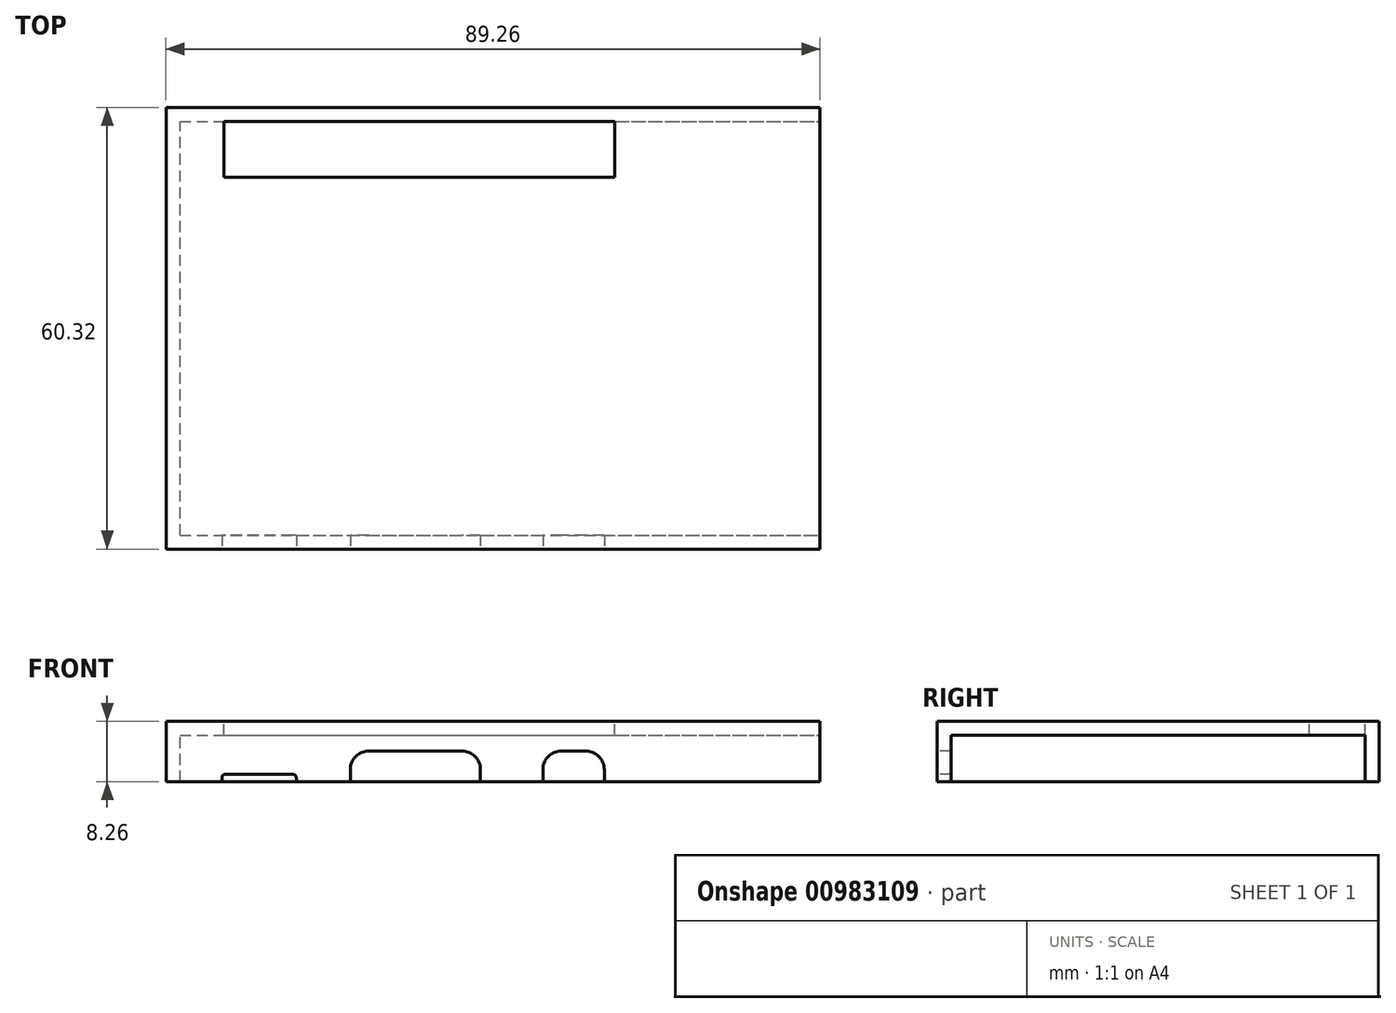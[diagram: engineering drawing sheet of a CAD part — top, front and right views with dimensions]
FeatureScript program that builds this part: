
annotation { "Feature Type Name" : "Feature", "Feature Type Description" : "" }
export const myFeature = defineFeature(function(context is Context, id is Id, definition is map)
    precondition{}
    {
        {
            var Q0;
            Q0=qCreatedBy(makeId("Top.planeOp"),FACE);
            var sketch = newSketch(context, id + "F0", { "sketchPlane" : qUnion([Q0])});
            skLineSegment(sketch, "E0.bottom", {"start": v(-44.63, -30.16) * mm, "end": v(44.63, -30.16) * mm});
            skLineSegment(sketch, "E0.top", {"start": v(-44.63, 30.16) * mm, "end": v(44.63, 30.16) * mm});
            skLineSegment(sketch, "E0.left", {"start": v(-44.63, -30.16) * mm, "end": v(-44.63, 30.16) * mm});
            skLineSegment(sketch, "E0.right", {"start": v(44.63, -30.16) * mm, "end": v(44.63, 30.16) * mm});
            skLineSegment(sketch, "E1", {"start": v(-44.63, 30.16) * mm, "end": v(44.63, -30.16) * mm, "construction": true});
            skSolve(sketch);
        }
        {
            var Q0;
            Q0=makeQuery(id+"F0.imprint","IMPRINT",FACE,{"disambiguationData":[TD([[makeQuery(id+"F0.imprint","IMPRINT",EDGE,{"derivedFrom":sQuery(id+"F0.wireOp",EDGE,"E0.bottom")}),1.0]])]});
            extrude(context, id + "F1", {"entities" : qUnion([Q0]), "depth" : 1.9 * mm, "offsetDistance" : 25.4 * mm});
        }
        {
            var Q0;
            Q0=makeQuery(id+"F1.opExtrude","CAP_FACE",FACE,{"disambiguationData":[OSD([sQuery(id+"F0.wireOp",EDGE,"E0.bottom"),sQuery(id+"F0.wireOp",EDGE,"E0.top"),sQuery(id+"F0.wireOp",EDGE,"E0.left"),sQuery(id+"F0.wireOp",EDGE,"E0.right")])],"isStart":true});
            var sketch = newSketch(context, id + "F2", { "sketchPlane" : qUnion([Q0])});
            skLineSegment(sketch, "E2.0", {"start": v(-42.72, 28.26) * mm, "end": v(44.63, 28.26) * mm});
            skLineSegment(sketch, "E2.1", {"start": v(-42.72, 28.26) * mm, "end": v(-42.72, -28.26) * mm});
            skLineSegment(sketch, "E2.2", {"start": v(-42.72, -28.26) * mm, "end": v(44.63, -28.26) * mm});
            skSolve(sketch);
        }
        {
            var Q0;
            Q0 = qSketchRegion(id + "F2", true);
            var Q1;
            {var subQ2=sQuery(id+"F2.wireOp",EDGE,"E2.0");Q1=makeQuery(id+"F2.imprint","IMPRINT",FACE,{"disambiguationData":[TD([[makeQuery(id+"F2.imprint","IMPRINT",EDGE,{"derivedFrom":subQ2}),1.0]])]});}
            extrude(context, id + "F3", {"entities" : qUnion([Q0, Q1]), "operationType" : NewBodyOperationType.ADD, "depth" : 6.35 * mm, "offsetDistance" : 25.4 * mm});
        }
        {
            var Q0;
            {var subQ0=sQuery(id+"F0.wireOp",EDGE,"E0.bottom");Q0=makeQuery(id+"F3.boolean.opBoolean","MERGE",FACE,{"derivedFrom":[makeQuery(id+"F1.opExtrude","SWEPT_FACE",FACE,{"disambiguationData":[OSD([subQ0])]}),makeQuery(id+"F3.opExtrude","SWEPT_FACE",FACE,{"disambiguationData":[OSD([subQ0])]})]});}
            var sketch = newSketch(context, id + "F4", { "sketchPlane" : qUnion([Q0])});
            skLineSegment(sketch, "E3.bottom", {"start": v(-37, -6.35) * mm, "end": v(-26.85, -6.35) * mm});
            skLineSegment(sketch, "E3.top", {"start": v(-37, 1.9) * mm, "end": v(-26.85, 1.9) * mm});
            skLineSegment(sketch, "E3.left", {"start": v(-37, -6.35) * mm, "end": v(-37, -5.84) * mm});
            skLineSegment(sketch, "E3.right", {"start": v(-26.85, -6.35) * mm, "end": v(-26.85, -5.84) * mm});
            skLineSegment(sketch, "E4", {"start": v(-37, 1.9) * mm, "end": v(-26.85, -6.35) * mm, "construction": true});
            skLineSegment(sketch, "E5.bottom", {"start": v(-19.48, -6.35) * mm, "end": v(-1.7, -6.35) * mm});
            skLineSegment(sketch, "E5.top", {"start": v(-19.48, 1.9) * mm, "end": v(-1.7, 1.9) * mm});
            skLineSegment(sketch, "E5.left", {"start": v(-19.48, -6.35) * mm, "end": v(-19.48, -4.7) * mm});
            skLineSegment(sketch, "E5.right", {"start": v(-1.7, -6.35) * mm, "end": v(-1.7, -4.7) * mm});
            skLineSegment(sketch, "E6.bottom", {"start": v(6.8, -6.35) * mm, "end": v(15.2, -6.35) * mm});
            skLineSegment(sketch, "E6.top", {"start": v(6.8, 1.9) * mm, "end": v(15.2, 1.9) * mm});
            skLineSegment(sketch, "E6.left", {"start": v(6.8, -6.35) * mm, "end": v(6.8, -4.7) * mm});
            skLineSegment(sketch, "E6.right", {"start": v(15.2, -6.35) * mm, "end": v(15.2, -4.7) * mm});
            skLineSegment(sketch, "E7", {"start": v(-19.48, 1.9) * mm, "end": v(-1.7, -6.35) * mm, "construction": true});
            skLineSegment(sketch, "E8", {"start": v(6.8, 1.9) * mm, "end": v(15.2, -6.35) * mm, "construction": true});
            skLineSegment(sketch, "E9", {"start": v(11, -2.22) * mm, "end": v(-44.63, -2.22) * mm, "construction": true});
            skPoint(sketch, "E10", {"position": v(-31.93, -2.22) * mm});
            skPoint(sketch, "E11", {"position": v(-10.6, -2.22) * mm});
            skLineSegment(sketch, "E12", {"start": v(-27.35, -5.33) * mm, "end": v(-36.5, -5.33) * mm});
            skLineSegment(sketch, "E13", {"start": v(-16.94, -2.16) * mm, "end": v(-4.24, -2.16) * mm});
            skLineSegment(sketch, "E14", {"start": v(12.65, -2.16) * mm, "end": v(9.35, -2.16) * mm});
            skArc(sketch, "E15.filletArc", {"start": v(-36.5, -5.33) * mm, "mid": v(-36.86, -5.48) * mm, "end": v(-37, -5.84) * mm});
            skArc(sketch, "E16.filletArc", {"start": v(-26.85, -5.84) * mm, "mid": v(-27, -5.48) * mm, "end": v(-27.35, -5.33) * mm});
            skArc(sketch, "E17.filletArc", {"start": v(-16.94, -2.16) * mm, "mid": v(-18.74, -2.9) * mm, "end": v(-19.48, -4.7) * mm});
            skArc(sketch, "E18.filletArc", {"start": v(-1.7, -4.7) * mm, "mid": v(-2.44, -2.9) * mm, "end": v(-4.24, -2.16) * mm});
            skArc(sketch, "E19.filletArc", {"start": v(9.35, -2.16) * mm, "mid": v(7.55, -2.9) * mm, "end": v(6.8, -4.7) * mm});
            skArc(sketch, "E20.filletArc", {"start": v(15.2, -4.7) * mm, "mid": v(14.45, -2.9) * mm, "end": v(12.65, -2.16) * mm});
            skSolve(sketch);
        }
        {
            var Q0;
            {var subQ0=sQuery(id+"F4.wireOp",EDGE,"E3.bottom");Q0=makeQuery(id+"F4.imprint","IMPRINT",FACE,{"disambiguationData":[TD([[makeQuery(id+"F4.imprint","IMPRINT",EDGE,{"derivedFrom":subQ0}),1.0]])]});}
            var Q1;
            {var subQ0=sQuery(id+"F4.wireOp",EDGE,"E5.bottom");Q1=makeQuery(id+"F4.imprint","IMPRINT",FACE,{"disambiguationData":[TD([[makeQuery(id+"F4.imprint","IMPRINT",EDGE,{"derivedFrom":subQ0}),1.0]])]});}
            var Q2;
            {var subQ1=sQuery(id+"F4.wireOp",EDGE,"E5.right");var subQ3=sQuery(id+"F4.wireOp",EDGE,"F6wx7LOh-tbb4-1j2T-QHw4-YU2DghOIFzcY");var subQ4=makeQuery(id+"F4.imprint","INTERSECT",VERTEX,{"derivedFrom":[subQ1,subQ3]});Q2=makeQuery(id+"F4.imprint","IMPRINT",FACE,{"disambiguationData":[TD([[makeQuery(id+"F4.imprint","IMPRINT",EDGE,{"disambiguationData":[TD([[subQ4,1.0]])],"derivedFrom":subQ3}),-1.0]])]});}
            var Q3;
            {var subQ0=sQuery(id+"F4.wireOp",EDGE,"E6.bottom");Q3=makeQuery(id+"F4.imprint","IMPRINT",FACE,{"disambiguationData":[TD([[makeQuery(id+"F4.imprint","IMPRINT",EDGE,{"derivedFrom":subQ0}),1.0]])]});}
            var Q4;
            {var subQ1=sQuery(id+"F4.wireOp",EDGE,"E6.right");var subQ3=sQuery(id+"F4.wireOp",EDGE,"F6wx7LOh-tbb4-1j2T-QHw4-YU2DghOIFzcY");var subQ4=makeQuery(id+"F4.imprint","INTERSECT",VERTEX,{"derivedFrom":[subQ1,subQ3]});Q4=makeQuery(id+"F4.imprint","IMPRINT",FACE,{"disambiguationData":[TD([[makeQuery(id+"F4.imprint","IMPRINT",EDGE,{"disambiguationData":[TD([[subQ4,1.0]])],"derivedFrom":subQ3}),-1.0]])]});}
            var Q5;
            {var subQ0=sQuery(id+"F4.wireOp",EDGE,"1wFk4sEF-Si3s-dVZx-gWUV-ik2z0e3l4tKB");var subQ1=sQuery(id+"F4.wireOp",EDGE,"E6.left");var subQ2=makeQuery(id+"F4.imprint","INTERSECT",VERTEX,{"derivedFrom":[subQ1,subQ0]});Q5=makeQuery(id+"F4.imprint","IMPRINT",FACE,{"disambiguationData":[TD([[makeQuery(id+"F4.imprint","IMPRINT",EDGE,{"disambiguationData":[TD([[subQ2,1.0]])],"derivedFrom":subQ1}),-1.0]])]});}
            extrude(context, id + "F5", {"entities" : qUnion([Q0, Q1, Q2, Q3, Q4, Q5]), "operationType" : NewBodyOperationType.REMOVE, "oppositeDirection" : true, "depth" : 25.4 * mm, "offsetDistance" : 25.4 * mm});
        }
        {
            var Q0;
            Q0=makeQuery(id+"F1.opExtrude","CAP_FACE",FACE,{"disambiguationData":[OSD([sQuery(id+"F0.wireOp",EDGE,"E0.bottom"),sQuery(id+"F0.wireOp",EDGE,"E0.top"),sQuery(id+"F0.wireOp",EDGE,"E0.left"),sQuery(id+"F0.wireOp",EDGE,"E0.right")])],"isStart":false});
            var sketch = newSketch(context, id + "F6", { "sketchPlane" : qUnion([Q0])});
            skLineSegment(sketch, "E21.bottom", {"start": v(-36.75, 28.26) * mm, "end": v(16.59, 28.26) * mm});
            skLineSegment(sketch, "E21.top", {"start": v(-36.75, 20.64) * mm, "end": v(16.59, 20.64) * mm});
            skLineSegment(sketch, "E21.left", {"start": v(-36.75, 28.26) * mm, "end": v(-36.75, 20.64) * mm});
            skLineSegment(sketch, "E21.right", {"start": v(16.59, 28.26) * mm, "end": v(16.59, 20.64) * mm});
            skLineSegment(sketch, "E22", {"start": v(-36.75, 20.64) * mm, "end": v(16.59, 28.26) * mm, "construction": true});
            skLineSegment(sketch, "E23", {"start": v(-10.08, 24.45) * mm, "end": v(-44.63, 24.45) * mm, "construction": true});
            skLineSegment(sketch, "E24", {"start": v(-10.08, 30.16) * mm, "end": v(-10.08, 24.45) * mm, "construction": true});
            skSolve(sketch);
        }
        {
            var Q0;
            Q0=makeQuery(id+"F6.imprint","IMPRINT",FACE,{"disambiguationData":[TD([[makeQuery(id+"F6.imprint","IMPRINT",EDGE,{"derivedFrom":sQuery(id+"F6.wireOp",EDGE,"E21.bottom")}),-1.0]])]});
            extrude(context, id + "F7", {"entities" : qUnion([Q0]), "operationType" : NewBodyOperationType.REMOVE, "oppositeDirection" : true, "depth" : 25.4 * mm, "offsetDistance" : 25.4 * mm});
        }
    });
